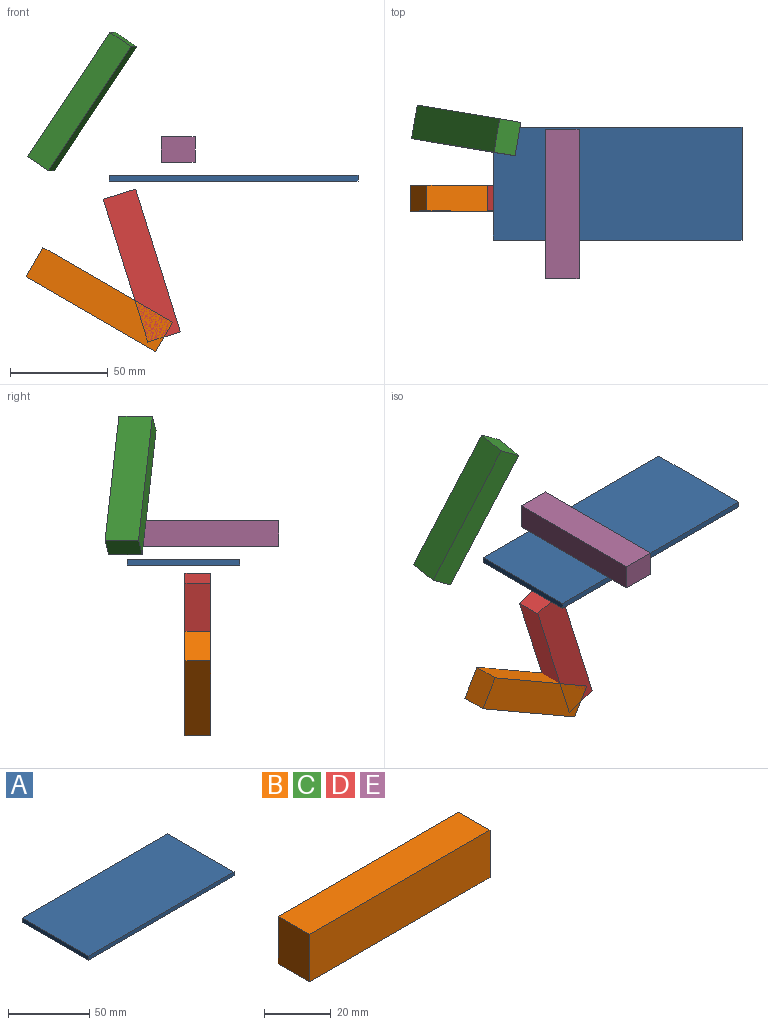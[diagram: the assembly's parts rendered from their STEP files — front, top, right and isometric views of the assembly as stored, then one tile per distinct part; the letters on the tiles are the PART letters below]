
ASSEMBLY  parts=5 mates=2
PART A: 6 faces, bbox 127x57.5x3 mm
  f0: plane 127x3.05mm, normal (0,1,0), area 387.1mm2, adj f1,f3,f4,f5
  f1: plane 57.52x3.05mm, normal (-1,0,0), area 175.3mm2, adj f0,f2,f4,f5
  f2: plane 127x3.05mm, normal (0,-1,0), area 387.1mm2, adj f1,f3,f4,f5
  f3: plane 57.52x3.05mm, normal (1,0,0), area 175.3mm2, adj f0,f2,f4,f5
  f4: plane 127x57.52mm, normal (0,0,1), area 7305.2mm2, adj f0,f1,f2,f3
  f5: plane 127x57.52mm, normal (0,0,-1), area 7305.2mm2, adj f0,f1,f2,f3
PART B: 6 faces, bbox 76.4x13.2x17.3 mm
  f0: plane 76.41x13.21mm, normal (0,0,1), area 1009.3mm2, adj f1,f3,f4,f5
  f1: plane 17.35x13.21mm, normal (-1,0,0), area 229.1mm2, adj f0,f2,f4,f5
  f2: plane 76.41x13.21mm, normal (0,0,-1), area 1009.3mm2, adj f1,f3,f4,f5
  f3: plane 17.35x13.21mm, normal (1,0,0), area 229.1mm2, adj f0,f2,f4,f5
  f4: plane 76.41x17.35mm, normal (0,-1,0), area 1325.4mm2, adj f0,f1,f2,f3
  f5: plane 76.41x17.35mm, normal (0,1,0), area 1325.4mm2, adj f0,f1,f2,f3
PART C: same geometry as B
PART D: same geometry as B
PART E: same geometry as B
PLACE A t=(14.73,-64.68,-40.11)mm
PLACE B rot(axis=(0,1,0),30deg) t=(-44.09,-19.12,-79.63)mm
PLACE C rot(axis=(-0.3,0.71,0.64),134.9deg) t=(25.4,-4.2,51.44)mm
PLACE D rot(axis=(0,1,0),72.7deg) t=(6.04,-19.12,-31.43)mm
PLACE E rot(axis=(0.58,-0.58,-0.58),120deg) t=(58.52,28.07,-17.36)mm
MATE ball B.f4 <-> D.f4  axis (0,-1,0) through (42.68,-32.32,-119.71)mm
MATE parallel E.f4 <-> A.f4  axis (0,0,-1) through (49.85,-28.91,-30.57)mm
